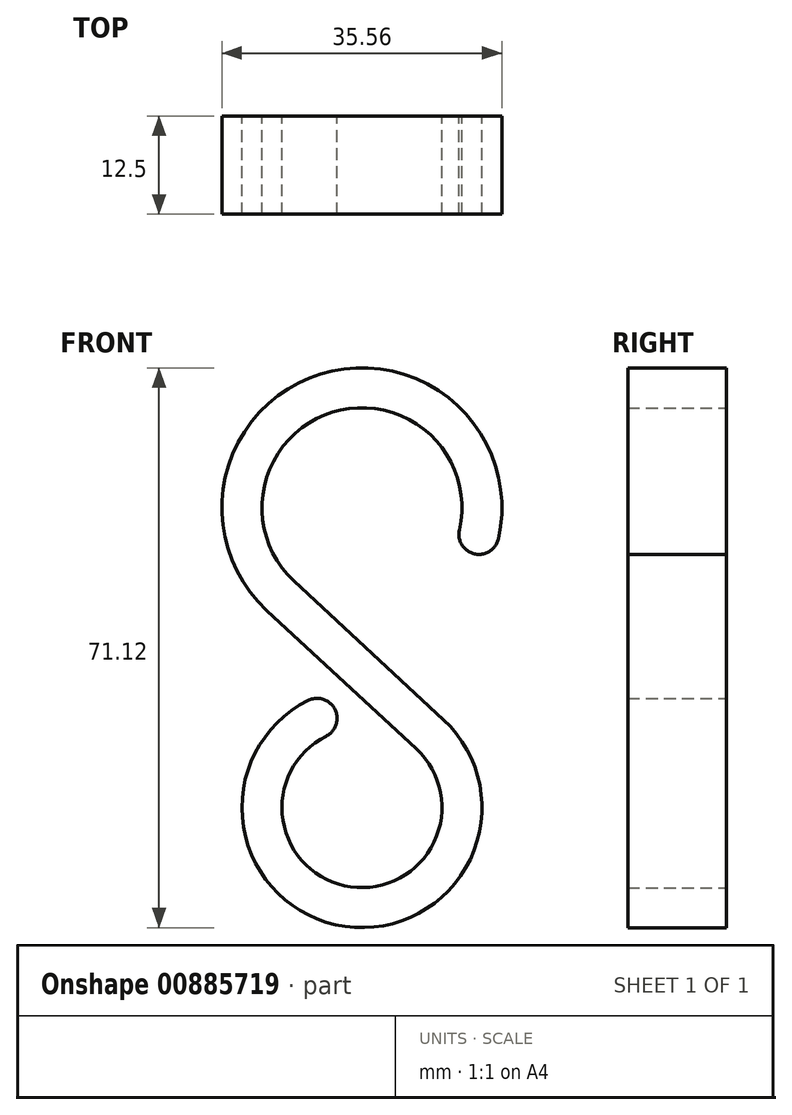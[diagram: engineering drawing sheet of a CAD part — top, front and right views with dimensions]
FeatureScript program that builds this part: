
annotation { "Feature Type Name" : "Feature", "Feature Type Description" : "" }
export const myFeature = defineFeature(function(context is Context, id is Id, definition is map)
    precondition{}
    {
        {
            var Q0;
            Q0=qCreatedBy(makeId("Front.planeOp"), FACE);
            var sketch = newSketch(context, id + "F0", { "sketchPlane" : qUnion([Q0])});
            skArc(sketch, "E0", {"start": v(12.38, -2.82) * mm, "mid": v(-3.75, 12.13) * mm, "end": v(-8.63, -9.31) * mm});
            skLineSegment(sketch, "E1", {"start": v(-8.63, -9.31) * mm, "end": v(10.36, -26.92) * mm});
            skArc(sketch, "E2", {"start": v(12.38, -2.82) * mm, "mid": v(14.3, -5.86) * mm, "end": v(17.34, -3.95) * mm});
            skArc(sketch, "E3", {"start": v(17.34, -3.95) * mm, "mid": v(-5.25, 16.99) * mm, "end": v(-12.09, -13.04) * mm});
            skLineSegment(sketch, "E4", {"start": v(0, 0) * mm, "end": v(14.86, -3.39) * mm, "construction": true});
            skLineSegment(sketch, "E5", {"start": v(0, 0) * mm, "end": v(-8.63, -9.31) * mm, "construction": true});
            skLineSegment(sketch, "E6", {"start": v(-12.09, -13.04) * mm, "end": v(6.9, -30.65) * mm});
            skArc(sketch, "E7", {"start": v(6.9, -30.65) * mm, "mid": v(-1.43, -48.16) * mm, "end": v(-4.56, -29.02) * mm});
            skArc(sketch, "E8", {"start": v(-4.56, -29.02) * mm, "mid": v(-3.43, -25.61) * mm, "end": v(-6.84, -24.48) * mm});
            skArc(sketch, "E9", {"start": v(-6.84, -24.48) * mm, "mid": v(-2.14, -53.19) * mm, "end": v(10.36, -26.92) * mm});
            skSolve(sketch);
        }
        {
            var Q0;
            Q0 = qSketchRegion(id + "F0", true);
            extrude(context, id + "F1", {"entities" : qUnion([Q0]), "domain" : OperationDomain.MODEL, "flatOperationType" : FlatOperationType.REMOVE, "depth" : 12.5 * mm, "offsetDistance" : 25.4 * mm});
        }
    });
